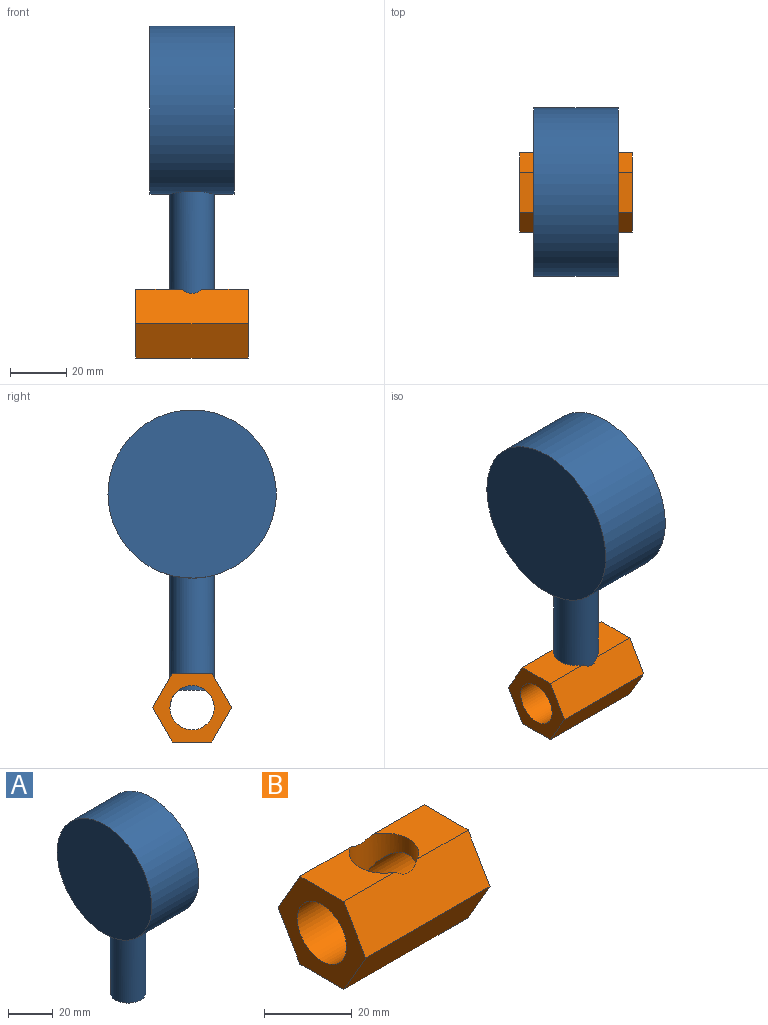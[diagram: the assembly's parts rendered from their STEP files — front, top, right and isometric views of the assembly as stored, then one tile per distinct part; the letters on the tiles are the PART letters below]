
ASSEMBLY  parts=2 mates=1
PART A: 5 faces, bbox 30x60x100 mm
  f0: cylinder r=30mm len=60mm, axis (-1,0,0), area 5457.2mm2, adj f1,f2,f3
  f1: plane 60x60mm, normal (1,0,0), area 2827.4mm2, adj f0
  f2: plane 60x60mm, normal (-1,0,0), area 2827.4mm2, adj f0
  f3: cylinder r=7.9mm len=41.06mm, axis (0,0,-1), area 2011.5mm2, adj f0,f4
  f4: plane 15.8x15.8mm, normal (0,0,-1), area 196mm2, adj f3
PART B: 11 faces, bbox 40x28.2x24.5 mm
  f0: plane 16.46x14.12mm, normal (0,0,1), area 188.5mm2, adj f3,f7,f8,f10
  f1: plane 16.46x14.12mm, normal (0,0,1), area 188.5mm2, adj f3,f7,f9,f10
  f2: cylinder r=7.9mm len=40mm, axis (1,0,0), area 1735.9mm2, adj f8,f9,f10
  f3: plane 40x12.23mm, normal (0,-0.87,0.5), area 557mm2, adj f0,f1,f4,f8,f9,f10
  f4: plane 40x12.23mm, normal (0,-0.87,-0.5), area 565mm2, adj f3,f5,f8,f9
  f5: plane 40x14.12mm, normal (0,0,-1), area 565mm2, adj f4,f6,f8,f9
  f6: plane 40x12.23mm, normal (0,0.87,-0.5), area 565mm2, adj f5,f7,f8,f9
  f7: plane 40x12.23mm, normal (0,0.87,0.5), area 557mm2, adj f0,f1,f6,f8,f9,f10
  f8: plane 28.25x24.46mm, normal (-1,0,0), area 322.2mm2, adj f0,f2,f3,f4,f5,f6,f7
  f9: plane 28.25x24.46mm, normal (1,0,0), area 322.2mm2, adj f1,f2,f3,f4,f5,f6,f7
  f10: cylinder r=7.9mm len=15.8mm, axis (0,0,1), area 343.4mm2, adj f0,f1,f2,f3,f7
PLACE A t=(-36.29,-17.94,50.74)mm
PLACE B t=(-16.29,-17.94,4.51)mm fixed
MATE revolute A.f3 <-> B.f10  axis (0,0,-1) through (-36.29,-17.94,10.74)mm
